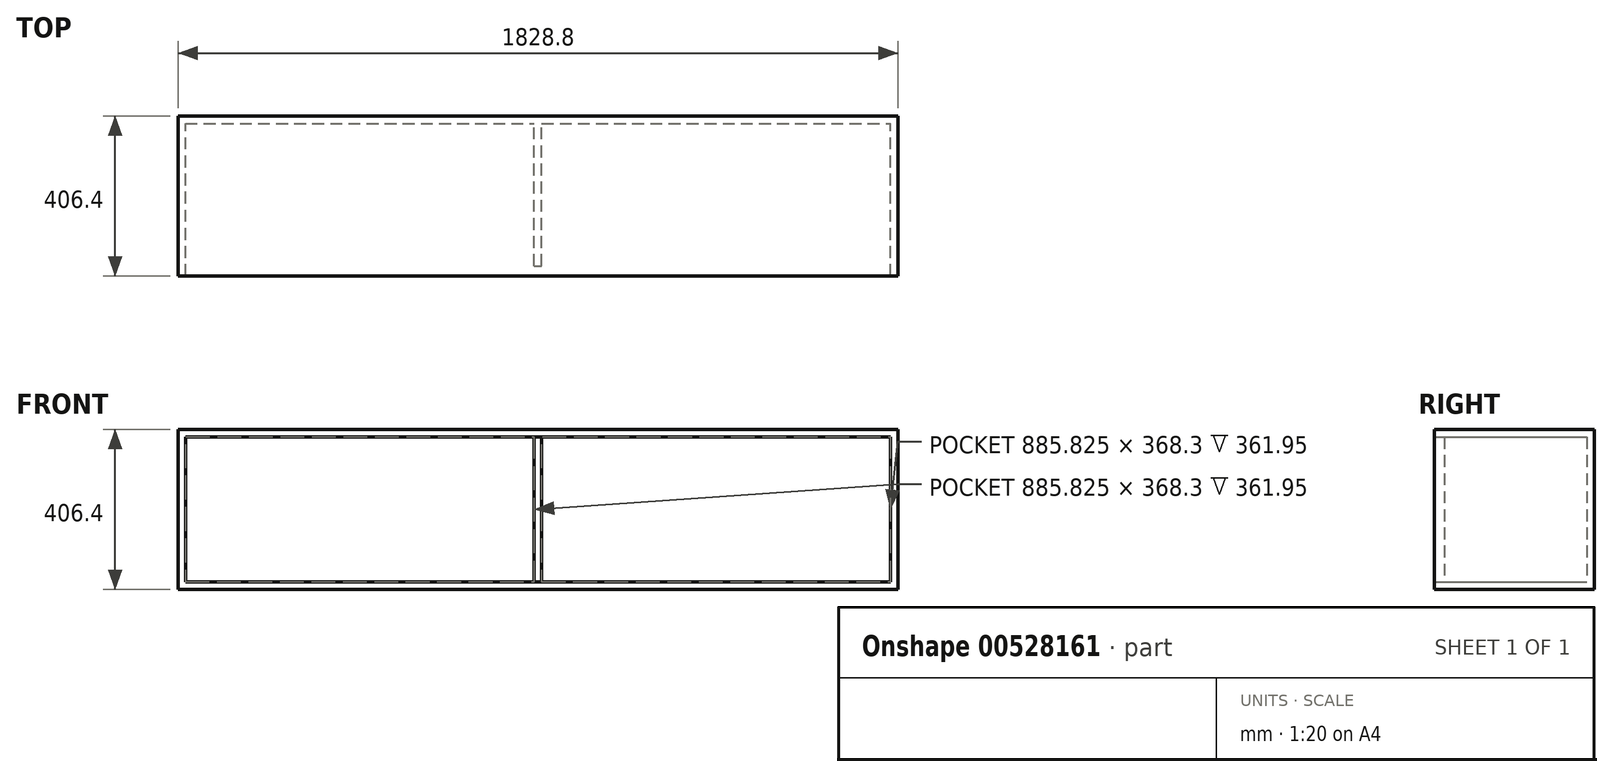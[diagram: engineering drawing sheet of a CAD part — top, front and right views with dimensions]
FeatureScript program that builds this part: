
annotation { "Feature Type Name" : "Feature", "Feature Type Description" : "" }
export const myFeature = defineFeature(function(context is Context, id is Id, definition is map)
    precondition{}
    {
        {
            var Q0;
            Q0=qCreatedBy(makeId("Front.planeOp"),FACE);
            var sketch = newSketch(context, id + "F0", { "sketchPlane" : qUnion([Q0])});
            skLineSegment(sketch, "E0.bottom", {"start": v(-914.4, 203.2) * mm, "end": v(914.4, 203.2) * mm});
            skLineSegment(sketch, "E0.top", {"start": v(-914.4, -203.2) * mm, "end": v(914.4, -203.2) * mm});
            skLineSegment(sketch, "E0.left", {"start": v(-914.4, 203.2) * mm, "end": v(-914.4, -203.2) * mm});
            skLineSegment(sketch, "E0.right", {"start": v(914.4, 203.2) * mm, "end": v(914.4, -203.2) * mm});
            skPoint(sketch, "E0.middle", {"position": v(0, 0) * mm});
            skSolve(sketch);
        }
        {
            var Q0;
            Q0=makeQuery(id+"F0.imprint","IMPRINT",FACE,{"disambiguationData":[TD([[makeQuery(id+"F0.imprint","IMPRINT",EDGE,{"derivedFrom":sQuery(id+"F0.wireOp",EDGE,"E0.bottom")}),-1.0]])]});
            extrude(context, id + "F1", {"entities" : qUnion([Q0]), "depth" : 406.4 * mm, "offsetDistance" : 25.4 * mm});
        }
        {
            var Q0;
            Q0=makeQuery(id+"F1.opExtrude","CAP_FACE",FACE,{"disambiguationData":[OSD([sQuery(id+"F0.wireOp",EDGE,"E0.bottom"),sQuery(id+"F0.wireOp",EDGE,"E0.top"),sQuery(id+"F0.wireOp",EDGE,"E0.left"),sQuery(id+"F0.wireOp",EDGE,"E0.right")])],"isStart":false});
            shell(context, id + "F2", {"entities" : qUnion([Q0]), "thickness" : 19.05 * mm});
        }
        {
            var Q0;
            Q0=makeQuery(id+"F2.opShell","OFFSET_FACE",FACE,{"disambiguationData":[OSD([sQuery(id+"F0.wireOp",EDGE,"E0.top")])]});
            var sketch = newSketch(context, id + "F3", { "sketchPlane" : qUnion([Q0])});
            skLineSegment(sketch, "E1.bottom", {"start": v(9.52, -406.4) * mm, "end": v(-9.52, -406.4) * mm});
            skLineSegment(sketch, "E1.top", {"start": v(9.52, -19.05) * mm, "end": v(-9.52, -19.05) * mm});
            skLineSegment(sketch, "E1.left", {"start": v(9.52, -406.4) * mm, "end": v(9.52, -19.05) * mm});
            skLineSegment(sketch, "E1.right", {"start": v(-9.52, -406.4) * mm, "end": v(-9.52, -19.05) * mm});
            skPoint(sketch, "E1.middle", {"position": v(0, -212.73) * mm});
            skSolve(sketch);
        }
        {
            var Q0;
            Q0=makeQuery(id+"F3.imprint","IMPRINT",FACE,{"disambiguationData":[TD([[makeQuery(id+"F3.imprint","IMPRINT",EDGE,{"derivedFrom":sQuery(id+"F3.wireOp",EDGE,"E1.bottom")}),1.0]])]});
            extrude(context, id + "F4", {"entities" : qUnion([Q0]), "operationType" : NewBodyOperationType.ADD, "depth" : 368.3 * mm, "offsetDistance" : 25.4 * mm});
        }
        {
            var Q0;
            Q0=makeQuery(id+"F4.boolean.opBoolean","MERGE",FACE,{"derivedFrom":[makeQuery(id+"F1.opExtrude","CAP_FACE",FACE,{"disambiguationData":[OSD([sQuery(id+"F0.wireOp",EDGE,"E0.bottom"),sQuery(id+"F0.wireOp",EDGE,"E0.top"),sQuery(id+"F0.wireOp",EDGE,"E0.left"),sQuery(id+"F0.wireOp",EDGE,"E0.right")])],"isStart":false}),makeQuery(id+"F4.opExtrude","SWEPT_FACE",FACE,{"disambiguationData":[OSD([sQuery(id+"F3.wireOp",EDGE,"E1.bottom")])]})]});
            var sketch = newSketch(context, id + "F5", { "sketchPlane" : qUnion([Q0])});
            skLineSegment(sketch, "E2", {"start": v(-9.52, 184.15) * mm, "end": v(9.52, 184.15) * mm});
            skLineSegment(sketch, "E3", {"start": v(-9.52, -184.15) * mm, "end": v(9.52, -184.15) * mm});
            skSolve(sketch);
        }
        {
            var Q0;
            Q0 = qSketchRegion(id + "F5", true);
            var Q1;
            Q1=makeQuery(id+"F5.imprint","IMPRINT",FACE,{"disambiguationData":[TD([[makeQuery(id+"F5.imprint","IMPRINT",EDGE,{"derivedFrom":sQuery(id+"F5.wireOp",EDGE,"E2")}),-1.0]])]});
            extrude(context, id + "F6", {"entities" : qUnion([Q0, Q1]), "operationType" : NewBodyOperationType.REMOVE, "oppositeDirection" : true, "depth" : 25.4 * mm, "offsetDistance" : 25.4 * mm});
        }
    });
